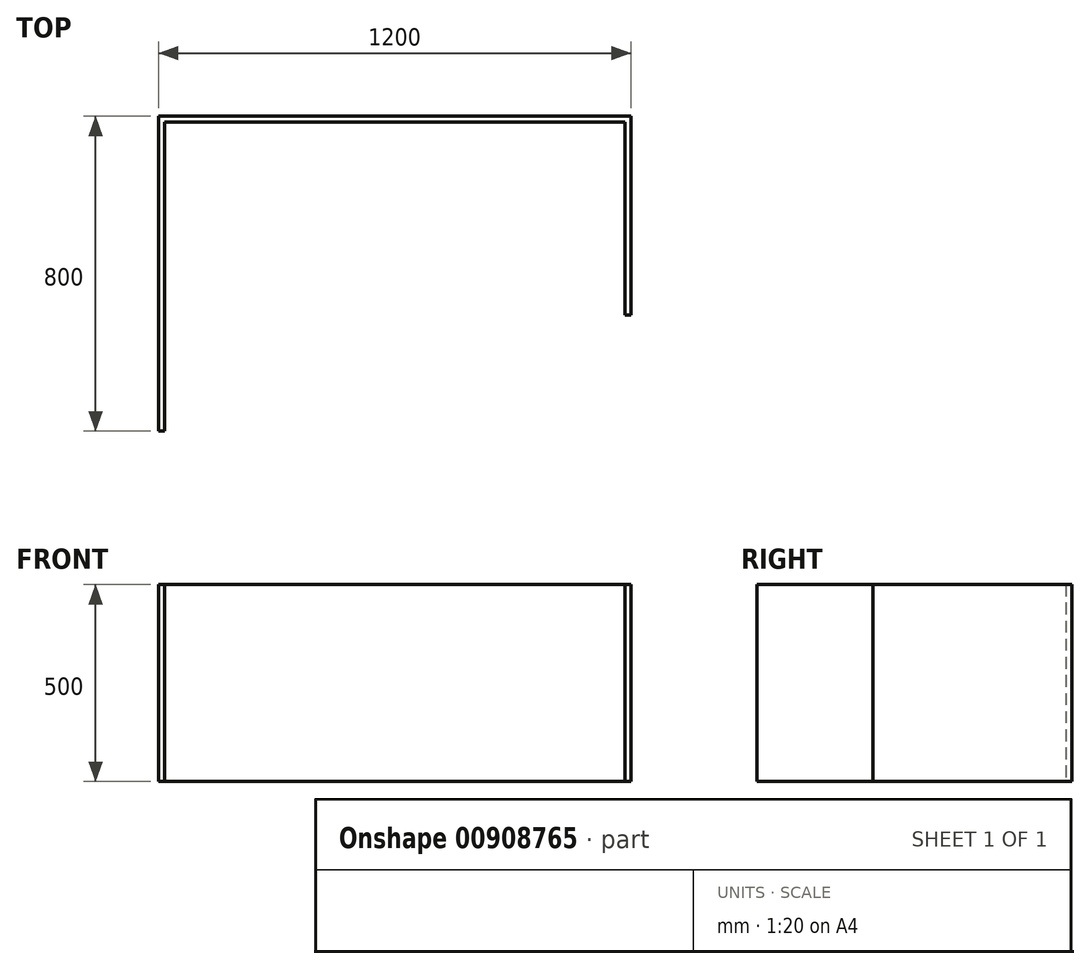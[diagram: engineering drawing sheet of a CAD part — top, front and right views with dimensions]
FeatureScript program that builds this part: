
annotation { "Feature Type Name" : "Feature", "Feature Type Description" : "" }
export const myFeature = defineFeature(function(context is Context, id is Id, definition is map)
    precondition{}
    {
        {
            var Q0;
            Q0=qCreatedBy(makeId("Top.planeOp"),FACE);
            var sketch = newSketch(context, id + "F0", { "sketchPlane" : qUnion([Q0])});
            skLineSegment(sketch, "E0.bottom", {"start": v(-596.4, 516.32) * mm, "end": v(603.6, 516.32) * mm});
            skLineSegment(sketch, "E0.top", {"start": v(-596.4, -283.68) * mm, "end": v(-269.57, -283.68) * mm});
            skLineSegment(sketch, "E0.left", {"start": v(-596.4, 516.32) * mm, "end": v(-596.4, -283.68) * mm});
            skLineSegment(sketch, "E0.right", {"start": v(603.6, 516.32) * mm, "end": v(603.6, 11.32) * mm});
            skLineSegment(sketch, "E1.top", {"start": v(603.6, 11.32) * mm, "end": v(573.6, 11.32) * mm});
            skLineSegment(sketch, "E1.right", {"start": v(-264.57, -278.68) * mm, "end": v(-264.57, -88.68) * mm});
            skPoint(sketch, "E2.visualSharp", {"position": v(-264.57, -283.68) * mm});
            skArc(sketch, "E2.filletArc", {"start": v(-269.57, -283.68) * mm, "mid": v(-266.03, -282.22) * mm, "end": v(-264.57, -278.68) * mm});
            skPoint(sketch, "E3.visualSharp", {"position": v(-264.57, 11.32) * mm});
            skArc(sketch, "E3.filletArc", {"start": v(-200.4, 4.68) * mm, "mid": v(-246.98, -32.04) * mm, "end": v(-264.57, -88.68) * mm});
            skArc(sketch, "E4", {"start": v(573.6, 11.32) * mm, "mid": v(186.35, 37.49) * mm, "end": v(-200.4, 4.68) * mm});
            skLineSegment(sketch, "E5.top", {"start": v(-596.4, 501.32) * mm, "end": v(603.6, 501.32) * mm});
            skLineSegment(sketch, "E5.left", {"start": v(-596.4, 516.32) * mm, "end": v(-596.4, 501.32) * mm});
            skLineSegment(sketch, "E5.right", {"start": v(603.6, 516.32) * mm, "end": v(603.6, 501.32) * mm});
            skLineSegment(sketch, "E6.bottom", {"start": v(603.6, 501.32) * mm, "end": v(588.6, 501.32) * mm});
            skLineSegment(sketch, "E6.top", {"start": v(603.6, 11.32) * mm, "end": v(588.6, 11.32) * mm});
            skLineSegment(sketch, "E6.left", {"start": v(603.6, 501.32) * mm, "end": v(603.6, 11.32) * mm});
            skLineSegment(sketch, "E6.right", {"start": v(588.6, 501.32) * mm, "end": v(588.6, 11.32) * mm});
            skLineSegment(sketch, "E7.bottom", {"start": v(-596.4, 501.32) * mm, "end": v(-581.4, 501.32) * mm});
            skLineSegment(sketch, "E7.top", {"start": v(-596.4, -283.68) * mm, "end": v(-581.4, -283.68) * mm});
            skLineSegment(sketch, "E7.left", {"start": v(-596.4, 501.32) * mm, "end": v(-596.4, -283.68) * mm});
            skLineSegment(sketch, "E7.right", {"start": v(-581.4, 501.32) * mm, "end": v(-581.4, -283.68) * mm});
            skSolve(sketch);
        }
        {
            var Q0;
            {var subQ0=sQuery(id+"F0.wireOp",EDGE,"E7.right");Q0=makeQuery(id+"F0.imprint","IMPRINT",FACE,{"disambiguationData":[TD([[makeQuery(id+"F0.imprint","IMPRINT",EDGE,{"derivedFrom":subQ0}),-1.0]])]});}
            var Q1;
            {var subQ4=sQuery(id+"F0.wireOp",EDGE,"E0.bottom");Q1=makeQuery(id+"F0.imprint","IMPRINT",FACE,{"disambiguationData":[TD([[makeQuery(id+"F0.imprint","IMPRINT",EDGE,{"derivedFrom":subQ4}),-1.0]])]});}
            var Q2;
            {var subQ5=sQuery(id+"F0.wireOp",EDGE,"E6.right");Q2=makeQuery(id+"F0.imprint","IMPRINT",FACE,{"disambiguationData":[TD([[makeQuery(id+"F0.imprint","IMPRINT",EDGE,{"derivedFrom":subQ5}),1.0]])]});}
            extrude(context, id + "F1", {"entities" : qUnion([Q0, Q1, Q2]), "depth" : 500 * mm, "offsetDistance" : 25 * mm});
        }
    });
